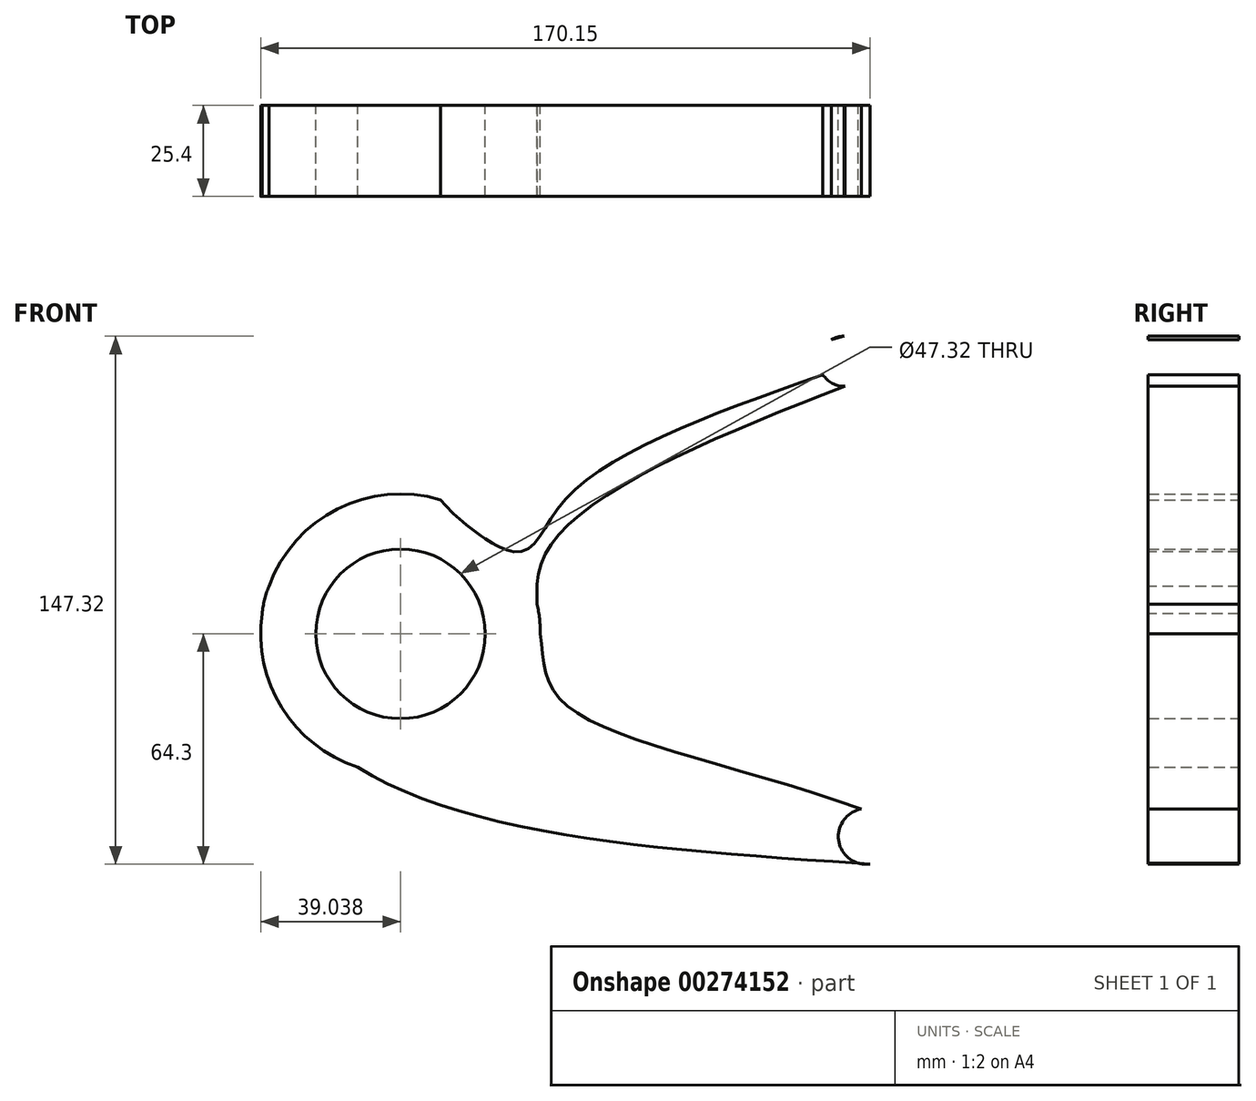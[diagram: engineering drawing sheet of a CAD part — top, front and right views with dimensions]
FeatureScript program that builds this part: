
annotation { "Feature Type Name" : "Feature", "Feature Type Description" : "" }
export const myFeature = defineFeature(function(context is Context, id is Id, definition is map)
    precondition{}
    {
        {
            var Q0;
            Q0=qCreatedBy(makeId("Front.planeOp"),FACE);
            var sketch = newSketch(context, id + "F0", { "sketchPlane" : qUnion([Q0])});
            skCircle(sketch, "E0", {"center": v(-47.9, 0) * mm, "radius": 23.66 * mm});
            skCircle(sketch, "E1", {"center": v(75.93, 76.04) * mm, "radius": 6.98 * mm});
            skCircle(sketch, "E2", {"center": v(82.07, -56.55) * mm, "radius": 7.75 * mm});
            skCircle(sketch, "E3", {"center": v(-47.9, 0) * mm, "radius": 39.04 * mm});
            skFitSpline(sketch, "E4", {"points": [v(75.93, 83.02) * mm, v(-57.8, 37.76) * mm, v(-86.52, 5.65) * mm, v(-59.88, -37.15) * mm, v(83.22, -64.22) * mm], "startDerivative": vector(-489.39, -135.33) * mm, "endDerivative": vector(523.66, -34.31) * mm});
            skFitSpline(sketch, "E5", {"points": [v(76.13, 69.06) * mm, v(-6.33, 24.23) * mm, v(-8.86, 0) * mm, v(-2.8, -18.8) * mm, v(80.7, -48.93) * mm], "startDerivative": vector(-312.35, -120.22) * mm, "endDerivative": vector(332.42, -119.16) * mm});
            skFitSpline(sketch, "E6", {"points": [v(68.94, 76.04) * mm, v(8.05, 58.48) * mm, v(-36.58, 39.73) * mm, v(-36.66, 37.38) * mm, v(-15.45, 22.82) * mm, v(-2.25, 37.09) * mm, v(70.02, 72.32) * mm], "startDerivative": vector(-255.23, -65.37) * mm, "endDerivative": vector(351.49, 124.52) * mm});
            skSolve(sketch);
        }
        {
            var Q0;
            {var subQ0=sQuery(id+"F0.wireOp",EDGE,"E5");var subQ1=sQuery(id+"F0.wireOp",EDGE,"E3");var subQ2=makeQuery(id+"F0.imprint","INTERSECT",VERTEX,{"disambiguationData":[OD(0.0)],"derivedFrom":[subQ1,subQ0]});Q0=makeQuery(id+"F0.imprint","IMPRINT",FACE,{"disambiguationData":[TD([[makeQuery(id+"F0.imprint","IMPRINT",EDGE,{"disambiguationData":[TD([[subQ2,1.0]])],"derivedFrom":subQ1}),1.0]])]});}
            var Q1;
            {var subQ0=sQuery(id+"F0.wireOp",EDGE,"E5");var subQ1=sQuery(id+"F0.wireOp",EDGE,"E1");var subQ2=makeQuery(id+"F0.imprint","INTERSECT",VERTEX,{"derivedFrom":[subQ1,subQ0]});Q1=makeQuery(id+"F0.imprint","IMPRINT",FACE,{"disambiguationData":[TD([[makeQuery(id+"F0.imprint","IMPRINT",EDGE,{"disambiguationData":[TD([[subQ2,1.0]])],"derivedFrom":subQ1}),-1.0]])]});}
            var Q2;
            {var subQ0=sQuery(id+"F0.wireOp",EDGE,"E5");var subQ1=sQuery(id+"F0.wireOp",EDGE,"E2");var subQ2=makeQuery(id+"F0.imprint","INTERSECT",VERTEX,{"derivedFrom":[subQ1,subQ0]});Q2=makeQuery(id+"F0.imprint","IMPRINT",FACE,{"disambiguationData":[TD([[makeQuery(id+"F0.imprint","IMPRINT",EDGE,{"disambiguationData":[TD([[subQ2,-1.0]])],"derivedFrom":subQ1}),-1.0]])]});}
            var Q3;
            Q3=makeQuery(id+"F0.imprint","IMPRINT",FACE,{"disambiguationData":[TD([[makeQuery(id+"F0.imprint","IMPRINT",EDGE,{"derivedFrom":sQuery(id+"F0.wireOp",EDGE,"E0")}),-1.0]])]});
            var Q4;
            {var subQ0=sQuery(id+"F0.wireOp",EDGE,"E4");var subQ1=sQuery(id+"F0.wireOp",EDGE,"E3");var subQ2=makeQuery(id+"F0.imprint","INTERSECT",VERTEX,{"disambiguationData":[OD(0.0)],"derivedFrom":[subQ1,subQ0]});Q4=makeQuery(id+"F0.imprint","IMPRINT",FACE,{"disambiguationData":[TD([[makeQuery(id+"F0.imprint","IMPRINT",EDGE,{"disambiguationData":[TD([[subQ2,-1.0]])],"derivedFrom":subQ1}),1.0]])]});}
            var Q5;
            {var subQ0=sQuery(id+"F0.wireOp",EDGE,"E4");var subQ1=sQuery(id+"F0.wireOp",EDGE,"E1");var subQ2=makeQuery(id+"F0.imprint","INTERSECT",VERTEX,{"disambiguationData":[OD(0.0)],"derivedFrom":[subQ1,subQ0]});Q5=makeQuery(id+"F0.imprint","IMPRINT",FACE,{"disambiguationData":[TD([[makeQuery(id+"F0.imprint","IMPRINT",EDGE,{"disambiguationData":[TD([[subQ2,-1.0]])],"derivedFrom":subQ1}),1.0]])]});}
            var Q6;
            {var subQ0=sQuery(id+"F0.wireOp",EDGE,"E4");var subQ1=sQuery(id+"F0.wireOp",EDGE,"E2");var subQ2=makeQuery(id+"F0.imprint","INTERSECT",VERTEX,{"disambiguationData":[OD(0.0)],"derivedFrom":[subQ1,subQ0]});Q6=makeQuery(id+"F0.imprint","IMPRINT",FACE,{"disambiguationData":[TD([[makeQuery(id+"F0.imprint","IMPRINT",EDGE,{"disambiguationData":[TD([[subQ2,1.0]])],"derivedFrom":subQ1}),1.0]])]});}
            var Q7;
            {var subQ0=sQuery(id+"F0.wireOp",EDGE,"E4");var subQ1=sQuery(id+"F0.wireOp",EDGE,"E3");var subQ2=makeQuery(id+"F0.imprint","INTERSECT",VERTEX,{"disambiguationData":[OD(2.0)],"derivedFrom":[subQ1,subQ0]});Q7=makeQuery(id+"F0.imprint","IMPRINT",FACE,{"disambiguationData":[TD([[makeQuery(id+"F0.imprint","IMPRINT",EDGE,{"disambiguationData":[TD([[subQ2,-1.0]])],"derivedFrom":subQ1}),1.0]])]});}
            var Q8;
            {var subQ0=sQuery(id+"F0.wireOp",EDGE,"E4");var subQ1=sQuery(id+"F0.wireOp",EDGE,"E3");var subQ2=makeQuery(id+"F0.imprint","INTERSECT",VERTEX,{"disambiguationData":[OD(1.0)],"derivedFrom":[subQ1,subQ0]});Q8=makeQuery(id+"F0.imprint","IMPRINT",FACE,{"disambiguationData":[TD([[makeQuery(id+"F0.imprint","IMPRINT",EDGE,{"disambiguationData":[TD([[subQ2,-1.0]])],"derivedFrom":subQ1}),-1.0]])]});}
            extrude(context, id + "F1", {"entities" : qUnion([Q0, Q1, Q2, Q3, Q4, Q5, Q6, Q7, Q8]), "depth" : 25.4 * mm});
        }
    });
